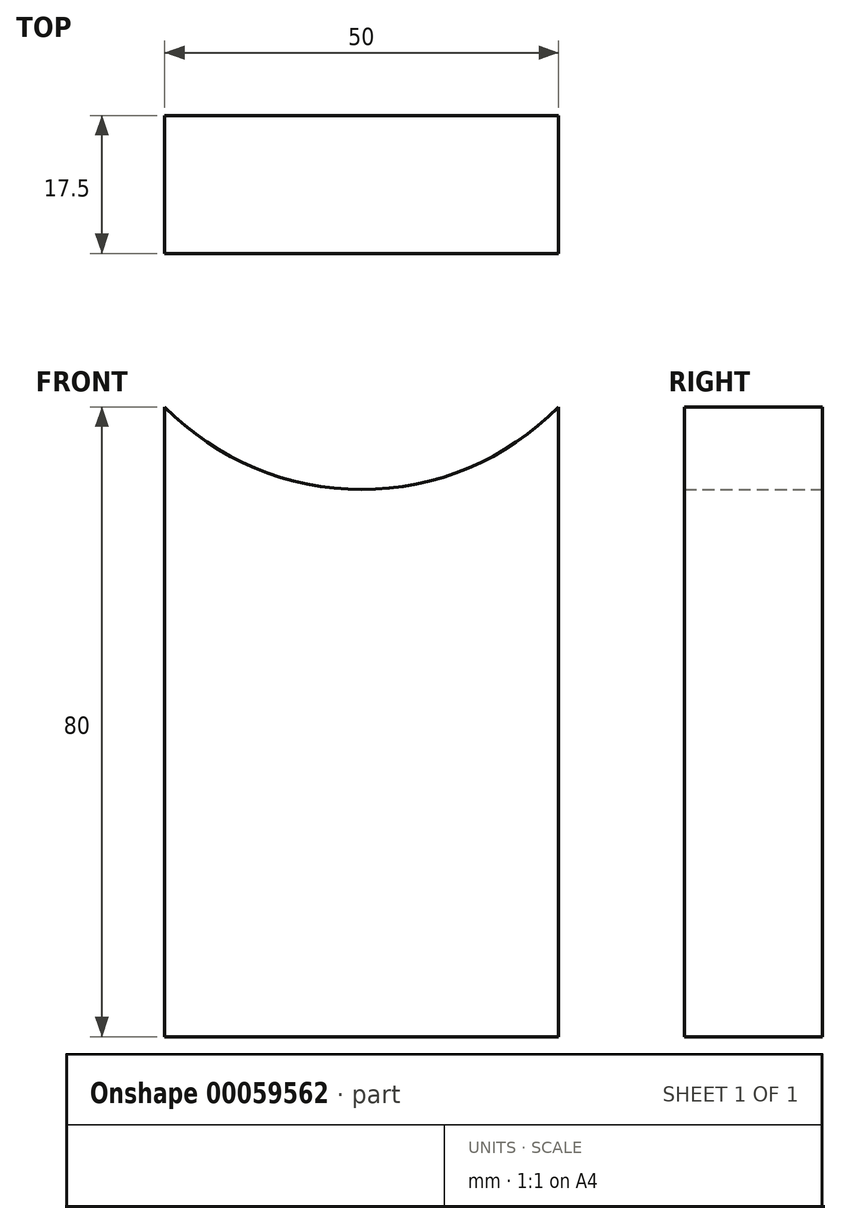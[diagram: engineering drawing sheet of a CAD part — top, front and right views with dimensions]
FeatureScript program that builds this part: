
annotation { "Feature Type Name" : "Feature", "Feature Type Description" : "" }
export const myFeature = defineFeature(function(context is Context, id is Id, definition is map)
    precondition{}
    {
        {
            var Q0;
            Q0=qCreatedBy(makeId("Front.planeOp"),FACE);
            var sketch = newSketch(context, id + "F0", { "sketchPlane" : qUnion([Q0])});
            skLineSegment(sketch, "E0.rect.top", {"start": v(-25, -40) * mm, "end": v(25, -40) * mm});
            skLineSegment(sketch, "E0.rect.left", {"start": v(-25, 40) * mm, "end": v(-25, -40) * mm});
            skLineSegment(sketch, "E0.rect.right", {"start": v(25, 40) * mm, "end": v(25, -40) * mm});
            skPoint(sketch, "E0.rect.middle", {"position": v(0, 0) * mm});
            skArc(sketch, "E1", {"start": v(-25, 40) * mm, "mid": v(0, 29.5) * mm, "end": v(25, 40) * mm});
            skSolve(sketch);
        }
        {
            var Q0;
            Q0=makeQuery(id+"F0.imprint","IMPRINT",FACE,{"disambiguationData":[TD([[makeQuery(id+"F0.imprint","IMPRINT",EDGE,{"derivedFrom":sQuery(id+"F0.wireOp",EDGE,"E0.rect.top")}),1.0]])]});
            extrude(context, id + "F1", {"entities" : qUnion([Q0]), "depth" : 17.5 * mm});
        }
    });
